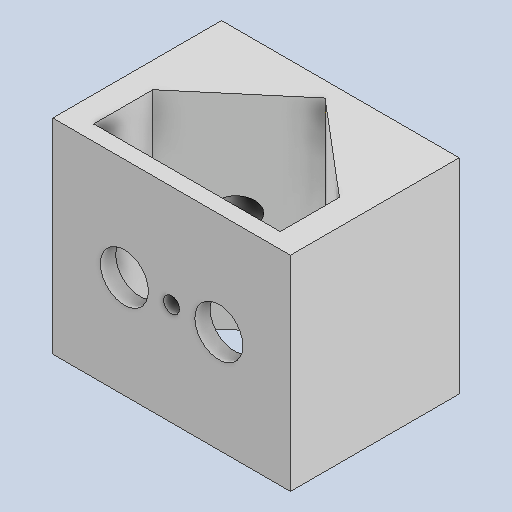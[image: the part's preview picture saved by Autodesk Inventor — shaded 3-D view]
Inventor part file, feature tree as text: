
AUTODESK INVENTOR PART (.ipt)
format: ipt  version: 2024.2 (Build 282272000, 272)  size: 181,248 bytes
history: native  units: mm
features: other x7, sketch x6, extrude x6, projected_geometry x2, reference x1
ambient origin geometry x8: Origin, YZ Plane, XZ Plane, XY Plane, X Axis, Y Axis, Z Axis, Center Point
bodies: Body1 (feature_tree)
feature tree (22):
  other  "Твердое тело1"
  other  "РабПлоскость2"
  sketch  "Эскиз1"
  extrude  "Выдавливание1"  Depth=4.0mm
  extrude  "Выдавливание2"  Depth=4.0mm
  other  "РабПлоскость4"
  extrude  "Выдавливание3"  Depth=3.0mm TaperAngle=0.0deg
  extrude  "Выдавливание4"  Depth=3.0mm TaperAngle=0.0deg
  extrude  "Выдавливание5"  Depth=3.0mm
  extrude  "Выдавливание6"  Depth=14.75mm TaperAngle=0.0deg
  reference  "Ссылка1"
  sketch  "Эскиз3"
  sketch  "Эскиз4"
  sketch  "Эскиз5"
  sketch  "Эскиз6"
  sketch  "Эскиз7"
  projected_geometry  "Спроецированная петля1"
  projected_geometry  "Спроецированная петля2"
  other  "<userpath>\Documents\Artist\3D\каретка.iam"
  other  "каретка.iam"
  other  "полное крепление каретки:1"
  other  "<userpath>\Documents\Artist\3D\каретка.iam"
